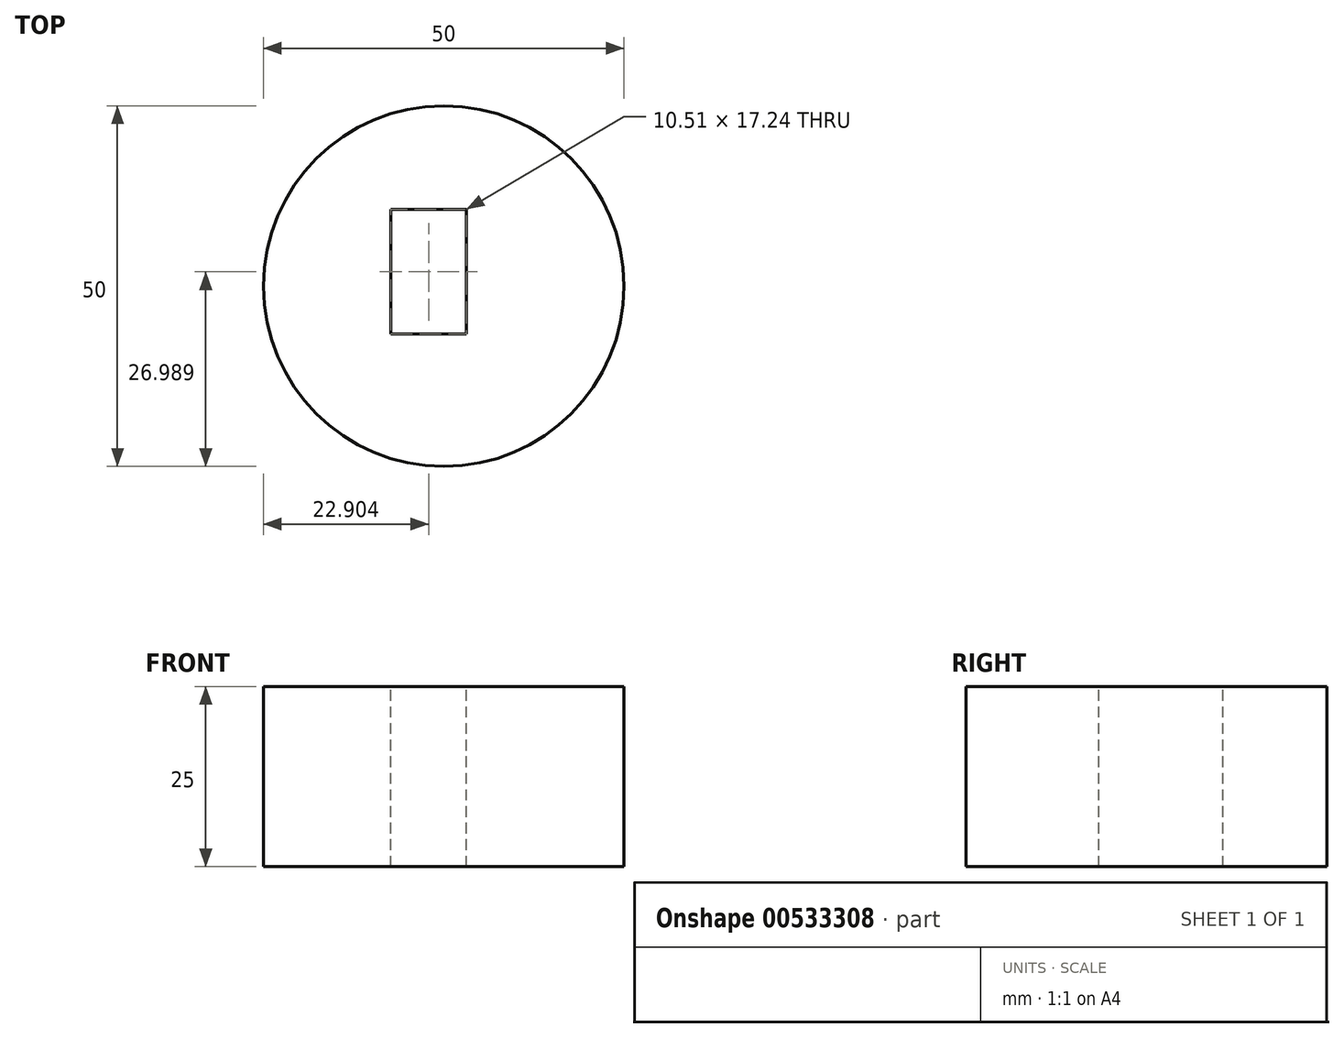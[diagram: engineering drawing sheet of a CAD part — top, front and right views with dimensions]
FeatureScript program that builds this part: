
annotation { "Feature Type Name" : "Feature", "Feature Type Description" : "" }
export const myFeature = defineFeature(function(context is Context, id is Id, definition is map)
    precondition{}
    {
        {
            var Q0;
            Q0=qCreatedBy(makeId("Top.planeOp"),FACE);
            var sketch = newSketch(context, id + "F0", { "sketchPlane" : qUnion([Q0])});
            skCircle(sketch, "E0", {"center": v(7.72, 0) * mm, "radius": 25 * mm});
            skSolve(sketch);
        }
        {
            var Q0;
            Q0=makeQuery(id+"F0.imprint","IMPRINT",FACE,{"disambiguationData":[TD([[makeQuery(id+"F0.imprint","IMPRINT",EDGE,{"derivedFrom":sQuery(id+"F0.wireOp",EDGE,"E0")}),1.0]])]});
            extrude(context, id + "F1", {"entities" : qUnion([Q0]), "depth" : 25 * mm, "offsetDistance" : 25 * mm});
        }
        {
            var Q0;
            Q0=makeQuery(id+"F1.opExtrude","CAP_FACE",FACE,{"disambiguationData":[OSD([sQuery(id+"F0.wireOp",EDGE,"E0")])],"isStart":false});
            var sketch = newSketch(context, id + "F2", { "sketchPlane" : qUnion([Q0])});
            skLineSegment(sketch, "E1.bottom", {"start": v(10.88, -6.63) * mm, "end": v(0.37, -6.63) * mm});
            skLineSegment(sketch, "E1.top", {"start": v(10.88, 10.6) * mm, "end": v(0.37, 10.6) * mm});
            skLineSegment(sketch, "E1.left", {"start": v(10.88, -6.63) * mm, "end": v(10.88, 10.6) * mm});
            skLineSegment(sketch, "E1.right", {"start": v(0.37, -6.63) * mm, "end": v(0.37, 10.6) * mm});
            skSolve(sketch);
        }
        {
            var Q0;
            Q0=makeQuery(id+"F2.imprint","IMPRINT",FACE,{"disambiguationData":[TD([[makeQuery(id+"F2.imprint","IMPRINT",EDGE,{"derivedFrom":sQuery(id+"F2.wireOp",EDGE,"E1.bottom")}),-1.0]])]});
            var sketch = newSketch(context, id + "F3", { "sketchPlane" : qUnion([Q0])});
            skSolve(sketch);
        }
        {
            var Q0;
            Q0=makeQuery(id+"F3.imprint","IMPRINT",FACE,{"disambiguationData":[TD([[makeQuery(id+"F3.imprint","IMPRINT",EDGE,{"derivedFrom":makeQuery(id+"F2.imprint","IMPRINT",EDGE,{"derivedFrom":sQuery(id+"F2.wireOp",EDGE,"E1.bottom")})}),-1.0]])]});
            extrude(context, id + "F4", {"entities" : qUnion([Q0]), "operationType" : NewBodyOperationType.REMOVE, "oppositeDirection" : true, "depth" : 31.96 * mm, "offsetDistance" : 25 * mm});
        }
    });
